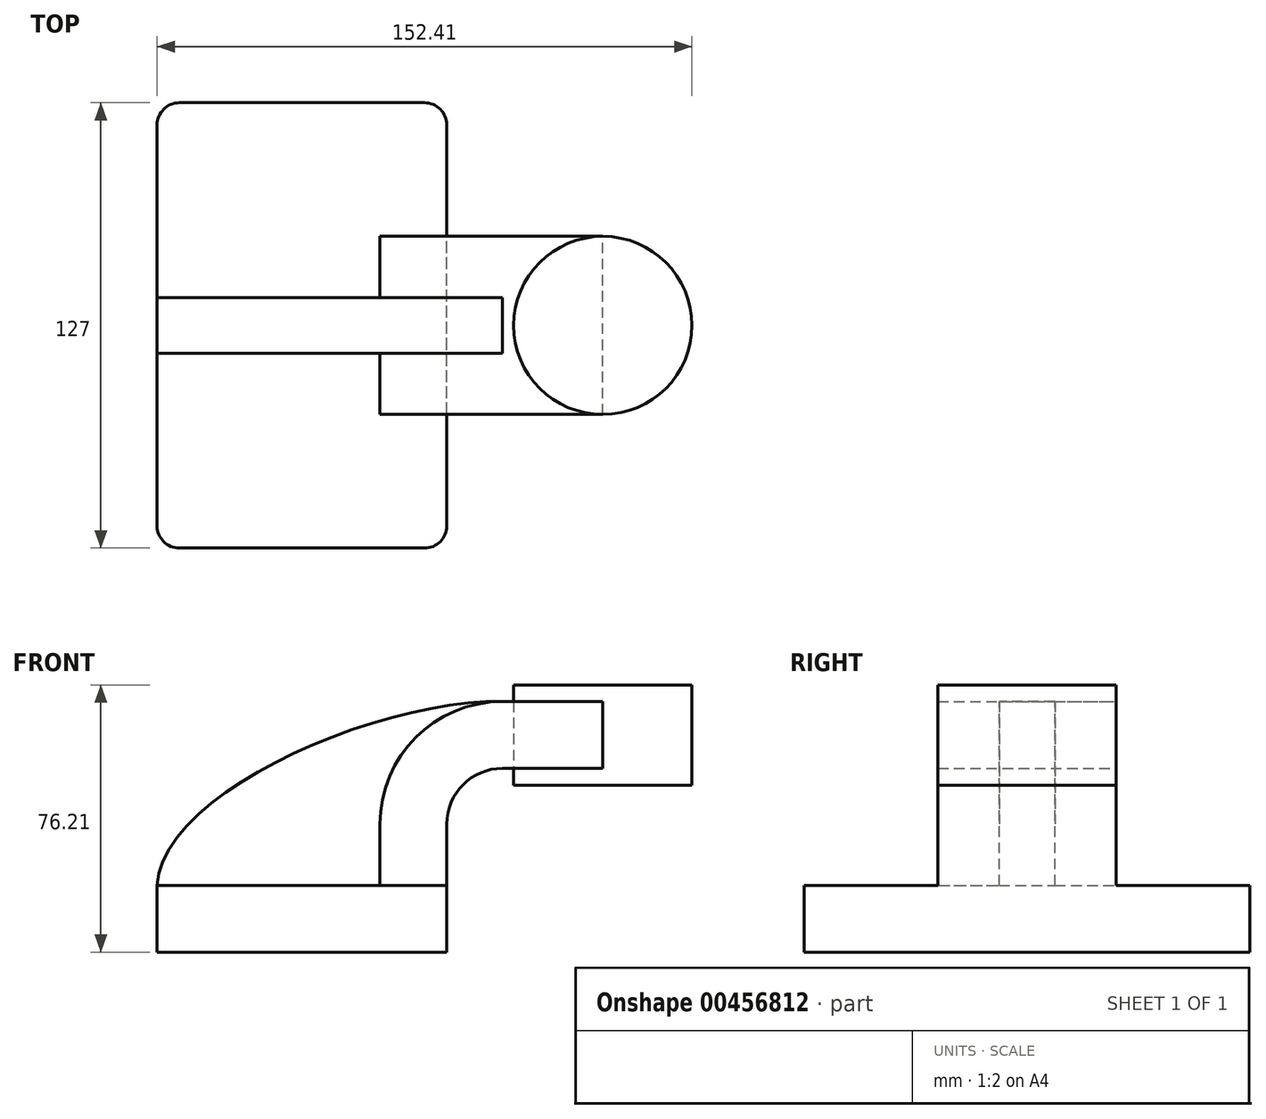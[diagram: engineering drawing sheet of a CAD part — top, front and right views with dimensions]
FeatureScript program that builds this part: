
annotation { "Feature Type Name" : "Feature", "Feature Type Description" : "" }
export const myFeature = defineFeature(function(context is Context, id is Id, definition is map)
    precondition{}
    {
        {
            var Q0;
            Q0=qCreatedBy(makeId("Front.planeOp"),FACE);
            var sketch = newSketch(context, id + "F0", { "sketchPlane" : qUnion([Q0])});
            skLineSegment(sketch, "E0.bottom", {"start": v(-41.28, -9.53) * mm, "end": v(41.28, -9.53) * mm});
            skLineSegment(sketch, "E0.top", {"start": v(-41.28, 9.53) * mm, "end": v(41.28, 9.53) * mm});
            skLineSegment(sketch, "E0.left", {"start": v(-41.28, -9.53) * mm, "end": v(-41.28, 9.53) * mm});
            skLineSegment(sketch, "E0.right", {"start": v(41.28, -9.53) * mm, "end": v(41.28, 9.53) * mm});
            skPoint(sketch, "E0.middle", {"position": v(0, 0) * mm});
            skLineSegment(sketch, "E1", {"start": v(41.28, 9.53) * mm, "end": v(41.28, 27) * mm});
            skArc(sketch, "E2", {"start": v(41.27, 27) * mm, "mid": v(45.92, 38.23) * mm, "end": v(57.15, 42.88) * mm});
            skLineSegment(sketch, "E3", {"start": v(57.15, 42.88) * mm, "end": v(85.72, 42.88) * mm});
            skLineSegment(sketch, "E4.bottom", {"start": v(60.32, 38.1) * mm, "end": v(111.12, 38.1) * mm});
            skLineSegment(sketch, "E4.top", {"start": v(60.32, 66.67) * mm, "end": v(111.12, 66.67) * mm});
            skLineSegment(sketch, "E4.left", {"start": v(60.32, 38.1) * mm, "end": v(60.32, 66.67) * mm});
            skLineSegment(sketch, "E4.right", {"start": v(111.12, 38.1) * mm, "end": v(111.12, 66.67) * mm});
            skPoint(sketch, "E4.middle", {"position": v(85.72, 52.39) * mm});
            skLineSegment(sketch, "E5.0", {"start": v(57.15, 61.93) * mm, "end": v(85.72, 61.93) * mm});
            skArc(sketch, "E5.1", {"start": v(22.22, 27) * mm, "mid": v(32.45, 51.7) * mm, "end": v(57.15, 61.93) * mm});
            skLineSegment(sketch, "E5.2", {"start": v(22.22, 9.53) * mm, "end": v(22.22, 27) * mm});
            skLineSegment(sketch, "E6", {"start": v(85.72, 38.1) * mm, "end": v(85.72, 66.67) * mm});
            skFitSpline(sketch, "E7", {"points": [v(-41.28, 9.53) * mm, v(57.15, 61.93) * mm], "startDerivative": vector(3.23, 79.03) * mm, "endDerivative": vector(106.26, -2.14) * mm});
            skSolve(sketch);
        }
        {
            var Q0;
            Q0=makeQuery(id+"F0.imprint","IMPRINT",FACE,{"disambiguationData":[TD([[makeQuery(id+"F0.imprint","IMPRINT",EDGE,{"derivedFrom":sQuery(id+"F0.wireOp",EDGE,"E0.bottom")}),1.0]])]});
            extrude(context, id + "F1", {"entities" : qUnion([Q0]), "endBound" : BoundingType.SYMMETRIC, "depth" : 127 * mm});
        }
        {
            var Q0;
            {var subQ7=sQuery(id+"F0.wireOp",EDGE,"E1");Q0=makeQuery(id+"F0.imprint","IMPRINT",FACE,{"disambiguationData":[TD([[makeQuery(id+"F0.imprint","IMPRINT",EDGE,{"derivedFrom":subQ7}),1.0]])]});}
            var Q1;
            {var subQ0=sQuery(id+"F0.wireOp",EDGE,"E6");var subQ1=sQuery(id+"F0.wireOp",EDGE,"E3");var subQ2=makeQuery(id+"F0.imprint","INTERSECT",VERTEX,{"derivedFrom":[subQ1,subQ0]});Q1=makeQuery(id+"F0.imprint","IMPRINT",FACE,{"disambiguationData":[TD([[makeQuery(id+"F0.imprint","IMPRINT",EDGE,{"disambiguationData":[TD([[subQ2,1.0]])],"derivedFrom":subQ1}),1.0]])]});}
            extrude(context, id + "F2", {"entities" : qUnion([Q0, Q1]), "operationType" : NewBodyOperationType.ADD, "endBound" : BoundingType.SYMMETRIC, "depth" : 50.8 * mm});
        }
        {
            var Q0;
            {var subQ3=sQuery(id+"F0.wireOp",EDGE,"E5.2");Q0=makeQuery(id+"F0.imprint","IMPRINT",FACE,{"disambiguationData":[TD([[makeQuery(id+"F0.imprint","IMPRINT",EDGE,{"derivedFrom":subQ3}),1.0]])]});}
            extrude(context, id + "F3", {"entities" : qUnion([Q0]), "operationType" : NewBodyOperationType.ADD, "endBound" : BoundingType.SYMMETRIC, "depth" : 15.88 * mm});
        }
        {
            var Q0;
            Q0=makeQuery(id+"F1.opExtrude","CAP_EDGE",EDGE,{"disambiguationData":[OSD([sQuery(id+"F0.wireOp",EDGE,"E0.left")])],"isStart":false});
            var Q1;
            Q1=makeQuery(id+"F1.opExtrude","CAP_EDGE",EDGE,{"disambiguationData":[OSD([sQuery(id+"F0.wireOp",EDGE,"E0.right")])],"isStart":false});
            var Q2;
            Q2=makeQuery(id+"F1.opExtrude","CAP_EDGE",EDGE,{"disambiguationData":[OSD([sQuery(id+"F0.wireOp",EDGE,"E0.right")])],"isStart":true});
            var Q3;
            Q3=makeQuery(id+"F1.opExtrude","CAP_EDGE",EDGE,{"disambiguationData":[OSD([sQuery(id+"F0.wireOp",EDGE,"E0.left")])],"isStart":true});
            fillet(context, id + "F4", {"entities" : qUnion([Q0, Q1, Q2, Q3]), "radius" : 6.35 * mm, "tangentPropagation" : true, "allowEdgeOverflow" : false});
        }
        {
            var Q0;
            {var subQ4=sQuery(id+"F0.wireOp",EDGE,"E4.right");Q0=makeQuery(id+"F0.imprint","IMPRINT",FACE,{"disambiguationData":[TD([[makeQuery(id+"F0.imprint","IMPRINT",EDGE,{"derivedFrom":subQ4}),1.0]])]});}
            var Q1;
            Q1=sQuery(id+"F0.wireOp",EDGE,"E6");
            revolve(context, id + "F5", {"entities" : qUnion([Q0]), "axis" : qUnion([Q1]), "revolveType" : RevolveType.FULL});
        }
    });
